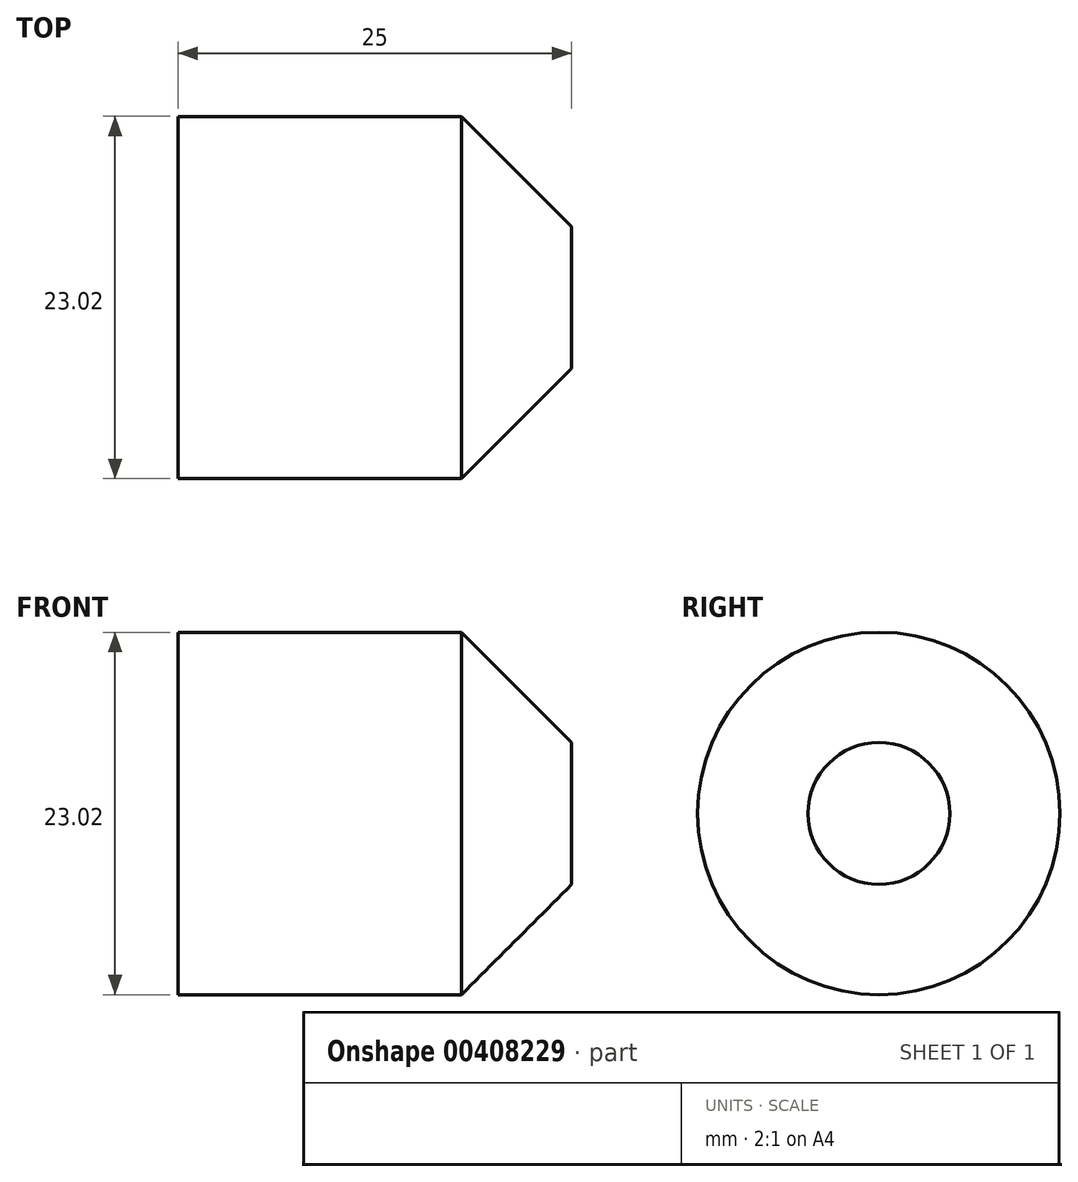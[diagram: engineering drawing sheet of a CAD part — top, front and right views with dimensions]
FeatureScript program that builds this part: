
annotation { "Feature Type Name" : "Feature", "Feature Type Description" : "" }
export const myFeature = defineFeature(function(context is Context, id is Id, definition is map)
    precondition{}
    {
        {
            var Q0;
            Q0=qCreatedBy(makeId("Right.planeOp"),FACE);
            var sketch = newSketch(context, id + "F0", { "sketchPlane" : qUnion([Q0])});
            skCircle(sketch, "E0", {"center": v(0, 0) * mm, "radius": 11.5 * mm});
            skSolve(sketch);
        }
        {
            var Q0;
            Q0=makeQuery(id+"F0.imprint","IMPRINT",FACE,{"disambiguationData":[TD([[makeQuery(id+"F0.imprint","IMPRINT",EDGE,{"derivedFrom":sQuery(id+"F0.wireOp",EDGE,"E0")}),1.0]])]});
            extrude(context, id + "F1", {"entities" : qUnion([Q0]), "depth" : 25 * mm});
        }
        {
            var Q0;
            Q0=makeQuery(id+"F1.opExtrude","CAP_FACE",FACE,{"disambiguationData":[OSD([sQuery(id+"F0.wireOp",EDGE,"E0")])],"isStart":false});
            chamfer(context, id + "F2", {"entities" : qUnion([Q0]), "width" : 7 * mm, "tangentPropagation" : true});
        }
    });
